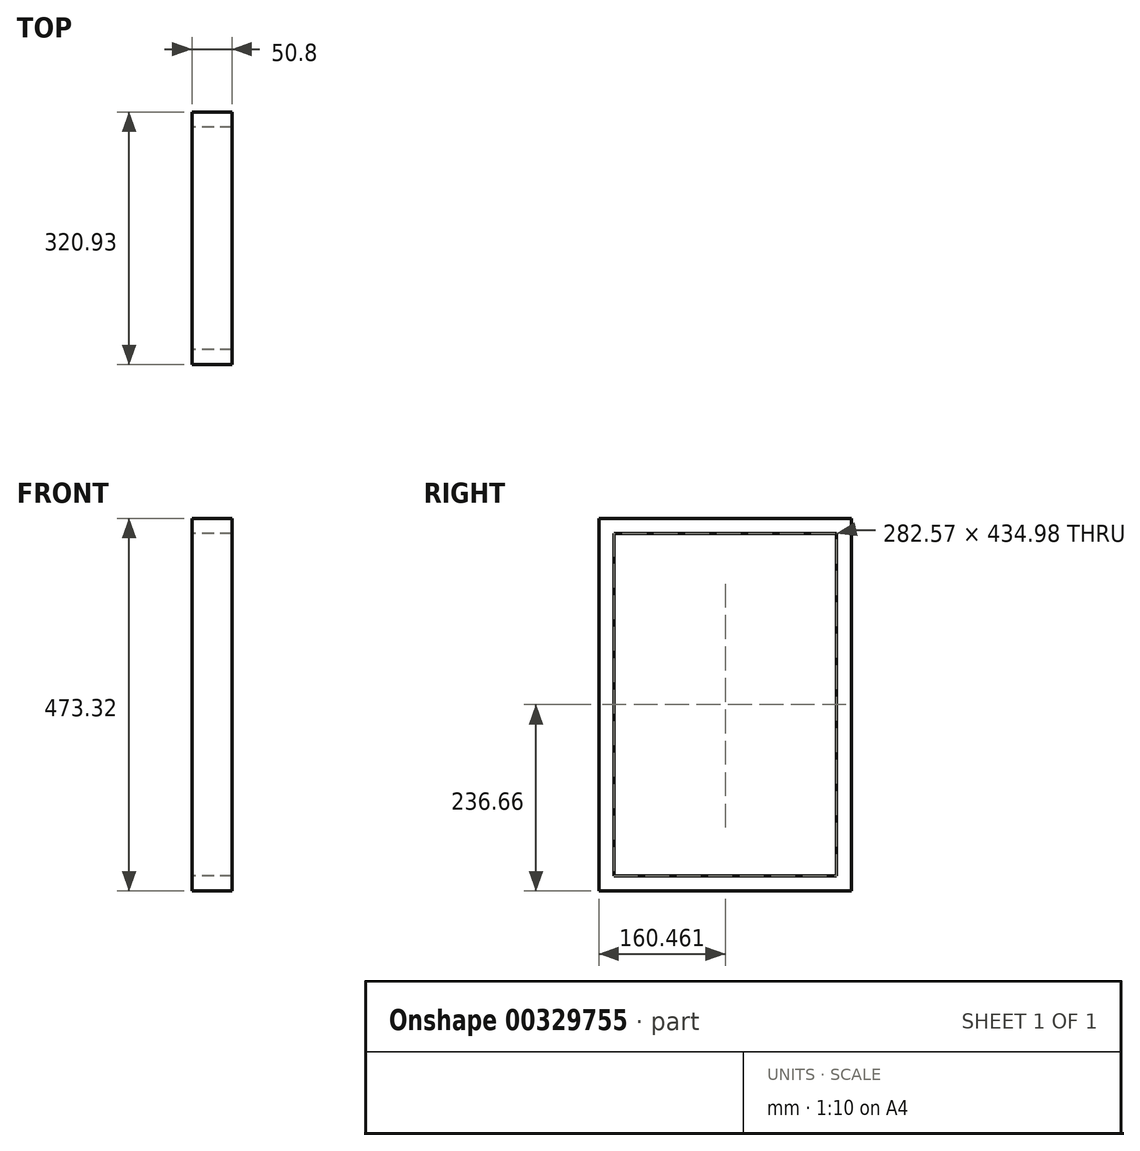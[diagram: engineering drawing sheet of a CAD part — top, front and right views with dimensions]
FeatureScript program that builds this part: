
annotation { "Feature Type Name" : "Feature", "Feature Type Description" : "" }
export const myFeature = defineFeature(function(context is Context, id is Id, definition is map)
    precondition{}
    {
        {
            var Q0;
            Q0=qCreatedBy(makeId("Right.planeOp"),FACE);
            var sketch = newSketch(context, id + "F0", { "sketchPlane" : qUnion([Q0])});
            skLineSegment(sketch, "E0.bottom", {"start": v(-140.48, 217.64) * mm, "end": v(142.1, 217.64) * mm});
            skLineSegment(sketch, "E0.top", {"start": v(-140.48, -217.34) * mm, "end": v(142.1, -217.34) * mm});
            skLineSegment(sketch, "E0.left", {"start": v(-140.48, 217.64) * mm, "end": v(-140.48, -217.34) * mm});
            skLineSegment(sketch, "E0.right", {"start": v(142.1, 217.64) * mm, "end": v(142.1, -217.34) * mm});
            skLineSegment(sketch, "E1.0", {"start": v(-159.65, 236.81) * mm, "end": v(161.28, 236.81) * mm});
            skLineSegment(sketch, "E2.0", {"start": v(-159.65, 236.81) * mm, "end": v(-159.65, -236.51) * mm});
            skLineSegment(sketch, "E3.0", {"start": v(161.28, 236.81) * mm, "end": v(161.28, -236.51) * mm});
            skLineSegment(sketch, "E4.0", {"start": v(-159.65, -236.51) * mm, "end": v(161.28, -236.51) * mm});
            skSolve(sketch);
        }
        {
            var Q0;
            Q0=makeQuery(id+"F0.imprint","IMPRINT",FACE,{"disambiguationData":[TD([[makeQuery(id+"F0.imprint","IMPRINT",EDGE,{"derivedFrom":sQuery(id+"F0.wireOp",EDGE,"E0.bottom")}),1.0]])]});
            extrude(context, id + "F1", {"entities" : qUnion([Q0]), "depth" : 50.8 * mm});
        }
    });
